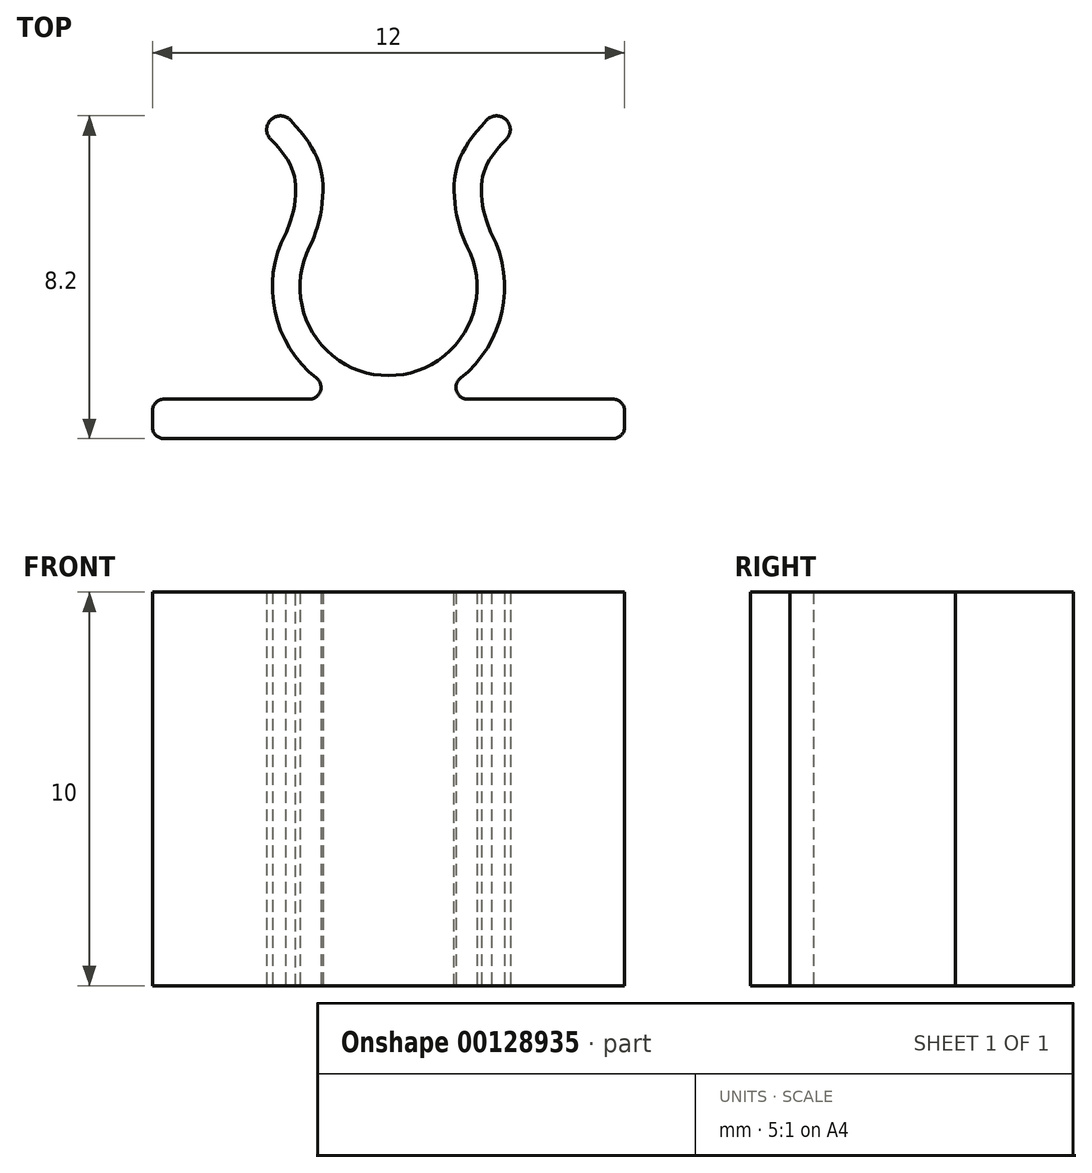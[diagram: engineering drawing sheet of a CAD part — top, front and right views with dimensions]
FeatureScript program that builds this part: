
annotation { "Feature Type Name" : "Feature", "Feature Type Description" : "" }
export const myFeature = defineFeature(function(context is Context, id is Id, definition is map)
    precondition{}
    {
        {
            var Q0;
            Q0=qCreatedBy(makeId("Top.planeOp"),FACE);
            var sketch = newSketch(context, id + "F0", { "sketchPlane" : qUnion([Q0])});
            skArc(sketch, "E0", {"start": v(-2, 1.03) * mm, "mid": v(0, -2.25) * mm, "end": v(2, 1.03) * mm});
            skArc(sketch, "E1", {"start": v(-2.62, 1.35) * mm, "mid": v(0, -2.95) * mm, "end": v(2.62, 1.35) * mm});
            skLineSegment(sketch, "E2", {"start": v(-2, 1.03) * mm, "end": v(-2.62, 1.35) * mm, "construction": true});
            skFitSpline(sketch, "E3", {"points": [v(-2, 1.03) * mm, v(-1.67, 2.62) * mm, v(-2.49, 4.24) * mm], "startDerivative": vector(1.28, 2.48) * mm, "endDerivative": vector(-3.2, 3.4) * mm});
            skLineSegment(sketch, "E4", {"start": v(0, -3.85) * mm, "end": v(0, 0) * mm, "construction": true});
            skFitSpline(sketch, "E5.0", {"points": [v(-2.62, 1.35) * mm, v(-2.59, 1.42) * mm, v(-2.51, 1.6) * mm, v(-2.42, 1.94) * mm, v(-2.36, 2.3) * mm, v(-2.36, 2.62) * mm, v(-2.4, 2.87) * mm, v(-2.5, 3.12) * mm, v(-2.68, 3.4) * mm, v(-2.88, 3.63) * mm, v(-3, 3.76) * mm]});
            skArc(sketch, "E6", {"start": v(-2.49, 4.24) * mm, "mid": v(-2.98, 4.26) * mm, "end": v(-3, 3.76) * mm});
            skArc(sketch, "E7.MirrorCS", {"start": v(2.49, 4.24) * mm, "mid": v(2.98, 4.26) * mm, "end": v(3, 3.76) * mm});
            skFitSpline(sketch, "E8.MirrorCS", {"points": [v(2, 1.03) * mm, v(1.67, 2.62) * mm, v(2.49, 4.24) * mm], "startDerivative": vector(-1.28, 2.48) * mm, "endDerivative": vector(3.2, 3.4) * mm});
            skLineSegment(sketch, "E9.MirrorCS", {"start": v(2, 1.03) * mm, "end": v(2.62, 1.35) * mm, "construction": true});
            skFitSpline(sketch, "E10.0", {"points": [v(2.62, 1.35) * mm, v(2.59, 1.42) * mm, v(2.51, 1.6) * mm, v(2.42, 1.94) * mm, v(2.36, 2.3) * mm, v(2.36, 2.62) * mm, v(2.4, 2.87) * mm, v(2.5, 3.12) * mm, v(2.68, 3.4) * mm, v(2.88, 3.63) * mm, v(3, 3.76) * mm]});
            skLineSegment(sketch, "E11.bottom", {"start": v(-6, -3.85) * mm, "end": v(6, -3.85) * mm});
            skLineSegment(sketch, "E11.top", {"start": v(-6, -2.85) * mm, "end": v(6, -2.85) * mm});
            skLineSegment(sketch, "E11.left", {"start": v(-6, -3.85) * mm, "end": v(-6, -2.85) * mm});
            skLineSegment(sketch, "E11.right", {"start": v(6, -3.85) * mm, "end": v(6, -2.85) * mm});
            skPoint(sketch, "E12", {"position": v(0, -3.85) * mm});
            skSolve(sketch);
        }
        {
            var Q0;
            Q0=makeQuery(id+"F0.imprint","IMPRINT",FACE,{"disambiguationData":[TD([[makeQuery(id+"F0.imprint","IMPRINT",EDGE,{"derivedFrom":sQuery(id+"F0.wireOp",EDGE,"E0")}),-1.0]])]});
            var Q1;
            Q1=makeQuery(id+"F0.imprint","IMPRINT",FACE,{"disambiguationData":[TD([[makeQuery(id+"F0.imprint","IMPRINT",EDGE,{"derivedFrom":sQuery(id+"F0.wireOp",EDGE,"E11.bottom")}),1.0]])]});
            var Q2;
            {var subQ0=sQuery(id+"F0.wireOp",EDGE,"E11.top");var subQ1=sQuery(id+"F0.wireOp",EDGE,"E1");var subQ2=makeQuery(id+"F0.imprint","INTERSECT",VERTEX,{"disambiguationData":[OD(0.0)],"derivedFrom":[subQ1,subQ0]});Q2=makeQuery(id+"F0.imprint","IMPRINT",FACE,{"disambiguationData":[TD([[makeQuery(id+"F0.imprint","IMPRINT",EDGE,{"disambiguationData":[TD([[subQ2,-1.0]])],"derivedFrom":subQ1}),1.0]])]});}
            extrude(context, id + "F1", {"entities" : qUnion([Q0, Q1, Q2]), "endBound" : BoundingType.SYMMETRIC, "depth" : 10 * mm});
        }
        {
            var Q0;
            Q0=makeQuery(id+"F1.opExtrude","SWEPT_EDGE",EDGE,{"disambiguationData":[OSD([sQuery(id+"F0.wireOp",EDGE,"E11.top"),sQuery(id+"F0.wireOp",EDGE,"E11.left")])]});
            var Q1;
            Q1=makeQuery(id+"F1.opExtrude","SWEPT_EDGE",EDGE,{"disambiguationData":[OSD([sQuery(id+"F0.wireOp",EDGE,"E11.bottom"),sQuery(id+"F0.wireOp",EDGE,"E11.left")])]});
            var Q2;
            Q2=makeQuery(id+"F1.opExtrude","SWEPT_EDGE",EDGE,{"disambiguationData":[OSD([sQuery(id+"F0.wireOp",EDGE,"E11.top"),sQuery(id+"F0.wireOp",EDGE,"E11.right")])]});
            var Q3;
            Q3=makeQuery(id+"F1.opExtrude","SWEPT_EDGE",EDGE,{"disambiguationData":[OSD([sQuery(id+"F0.wireOp",EDGE,"E11.bottom"),sQuery(id+"F0.wireOp",EDGE,"E11.right")])]});
            var Q4;
            {var subQ0=sQuery(id+"F0.wireOp",EDGE,"E11.top");var subQ1=sQuery(id+"F0.wireOp",EDGE,"E1");Q4=makeQuery(id+"F1.opExtrude","SWEPT_EDGE",EDGE,{"disambiguationData":[OSD([subQ1,subQ0]),TDD([makeQuery(id+"F0.imprint","INTERSECT",VERTEX,{"disambiguationData":[OD(1.0)],"derivedFrom":[subQ1,subQ0]})])]});}
            var Q5;
            {var subQ0=sQuery(id+"F0.wireOp",EDGE,"E11.top");var subQ1=sQuery(id+"F0.wireOp",EDGE,"E1");Q5=makeQuery(id+"F1.opExtrude","SWEPT_EDGE",EDGE,{"disambiguationData":[OSD([subQ1,subQ0]),TDD([makeQuery(id+"F0.imprint","INTERSECT",VERTEX,{"disambiguationData":[OD(0.0)],"derivedFrom":[subQ1,subQ0]})])]});}
            fillet(context, id + "F2", {"entities" : qUnion([Q0, Q1, Q2, Q3, Q4, Q5]), "radius" : 0.3 * mm, "tangentPropagation" : true, "allowEdgeOverflow" : false});
        }
    });
